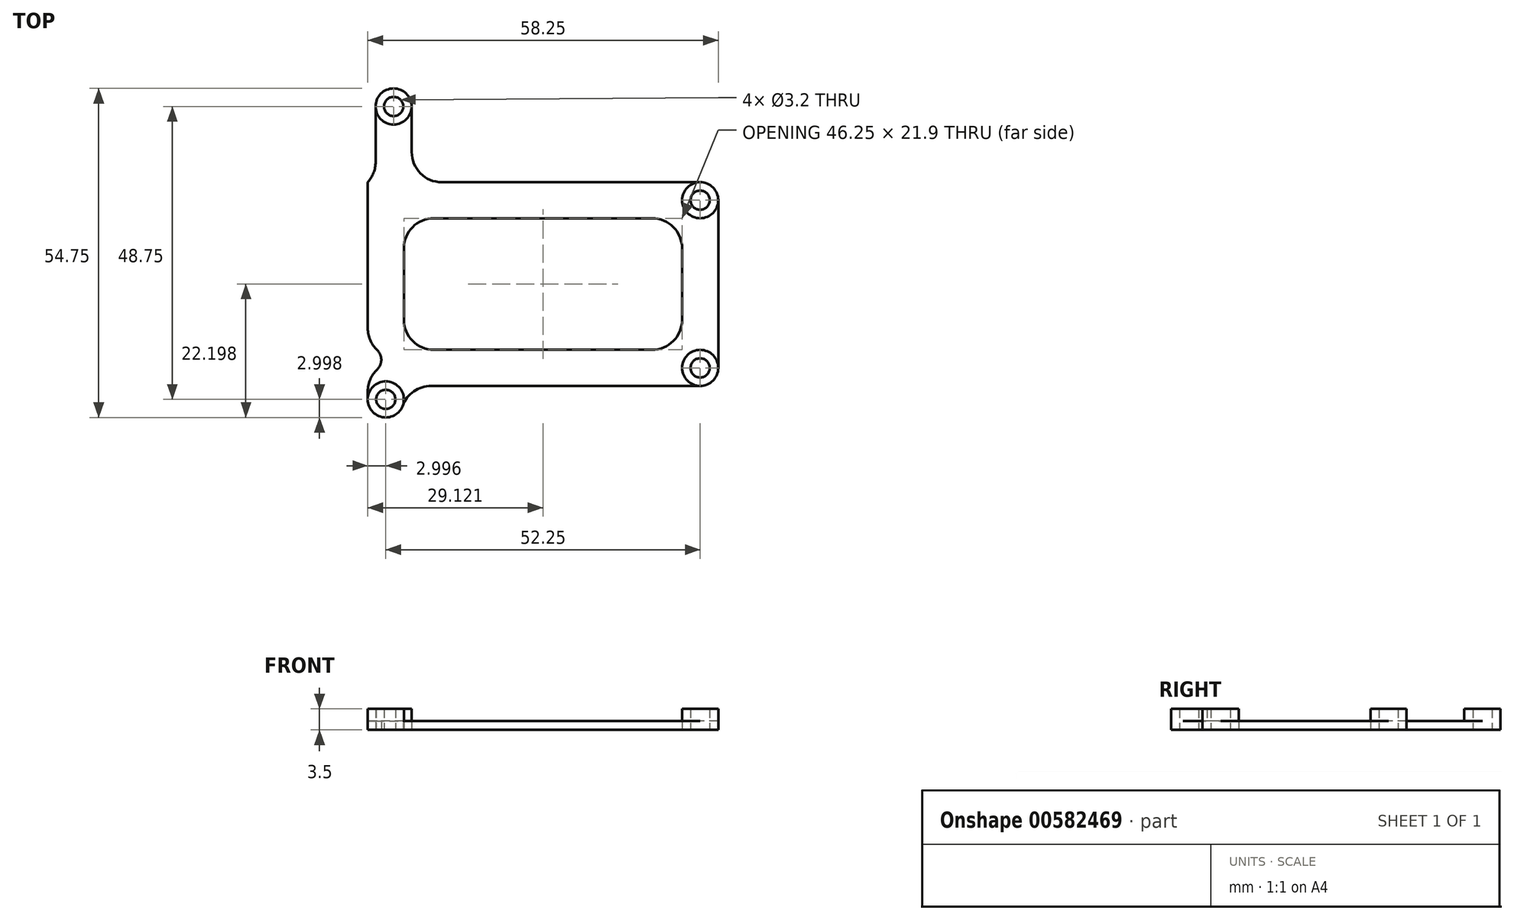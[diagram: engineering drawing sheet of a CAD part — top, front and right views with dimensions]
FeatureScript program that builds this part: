
annotation { "Feature Type Name" : "Feature", "Feature Type Description" : "" }
export const myFeature = defineFeature(function(context is Context, id is Id, definition is map)
    precondition{}
    {
        {
            var Q0;
            Q0=qCreatedBy(makeId("Top.planeOp"),FACE);
            var sketch = newSketch(context, id + "F0", { "sketchPlane" : qUnion([Q0])});
            skLineSegment(sketch, "E0.bottom", {"start": v(-21.9, 24.36) * mm, "end": v(30.35, 24.36) * mm, "construction": true});
            skLineSegment(sketch, "E0.top", {"start": v(-21.9, -24.4) * mm, "end": v(30.35, -24.4) * mm, "construction": true});
            skLineSegment(sketch, "E0.left", {"start": v(-21.9, 24.36) * mm, "end": v(-21.9, -24.4) * mm, "construction": true});
            skLineSegment(sketch, "E0.right", {"start": v(30.35, 24.36) * mm, "end": v(30.35, -24.4) * mm, "construction": true});
            skLineSegment(sketch, "E1", {"start": v(27.28, -19.14) * mm, "end": v(31.82, -19.14) * mm, "construction": true});
            skLineSegment(sketch, "E2", {"start": v(26.18, 8.76) * mm, "end": v(34.25, 8.76) * mm, "construction": true});
            skCircle(sketch, "E3", {"center": v(30.35, 8.76) * mm, "radius": 1.6 * mm});
            skCircle(sketch, "E4", {"center": v(30.35, -19.14) * mm, "radius": 1.6 * mm});
            skCircle(sketch, "E5", {"center": v(-21.9, -24.4) * mm, "radius": 1.6 * mm});
            skPoint(sketch, "E6.rect.middle", {"position": v(-21.9, 0) * mm});
            skLineSegment(sketch, "E7.bottom", {"start": v(30.35, 11.76) * mm, "end": v(-24.9, 11.76) * mm});
            skLineSegment(sketch, "E7.top", {"start": v(30.35, -22.14) * mm, "end": v(-18.9, -22.14) * mm});
            skLineSegment(sketch, "E7.left", {"start": v(33.35, 8.76) * mm, "end": v(33.35, -19.14) * mm});
            skLineSegment(sketch, "E7.right", {"start": v(-18.9, 11.76) * mm, "end": v(-18.9, -22.14) * mm});
            skLineSegment(sketch, "E8.bottom", {"start": v(-18.9, 5.76) * mm, "end": v(27.35, 5.76) * mm});
            skLineSegment(sketch, "E8.top", {"start": v(-18.9, -16.14) * mm, "end": v(27.35, -16.14) * mm});
            skLineSegment(sketch, "E8.left", {"start": v(-18.9, 5.76) * mm, "end": v(-18.9, -16.14) * mm});
            skLineSegment(sketch, "E8.right", {"start": v(27.35, 5.76) * mm, "end": v(27.35, -16.14) * mm});
            skCircle(sketch, "E9", {"center": v(-21.9, -24.4) * mm, "radius": 3 * mm});
            skCircle(sketch, "E10", {"center": v(30.35, 8.76) * mm, "radius": 3 * mm});
            skCircle(sketch, "E11", {"center": v(30.35, -19.14) * mm, "radius": 3 * mm});
            skLineSegment(sketch, "E12", {"start": v(-20.6, 24.36) * mm, "end": v(-20.6, 34.98) * mm, "construction": true});
            skCircle(sketch, "E13", {"center": v(-20.6, 24.36) * mm, "radius": 1.6 * mm});
            skPoint(sketch, "E14.orphan", {"position": v(-24.9, 28.63) * mm});
            skLineSegment(sketch, "E15.trimOffspring", {"start": v(-18.9, 11.76) * mm, "end": v(-18.9, -24.4) * mm});
            skPoint(sketch, "E6.rect.left.start.orphan", {"position": v(-18.9, 28.63) * mm});
            skCircle(sketch, "E16", {"center": v(-20.6, 24.36) * mm, "radius": 3 * mm});
            skLineSegment(sketch, "E17.top", {"start": v(-23.6, 11.76) * mm, "end": v(-17.6, 11.76) * mm});
            skLineSegment(sketch, "E17.left", {"start": v(-23.6, 24.36) * mm, "end": v(-23.6, 11.76) * mm});
            skLineSegment(sketch, "E17.right", {"start": v(-17.6, 24.36) * mm, "end": v(-17.6, 11.76) * mm});
            skLineSegment(sketch, "E18", {"start": v(-24.9, -24.4) * mm, "end": v(-24.9, -20.04) * mm});
            skPoint(sketch, "E19.orphan", {"position": v(-24.9, -28.63) * mm});
            skPoint(sketch, "E20.orphan", {"position": v(-18.9, -28.63) * mm});
            skArc(sketch, "E21", {"start": v(-24.9, -20.04) * mm, "mid": v(-22.65, -17.8) * mm, "end": v(-24.9, -15.54) * mm});
            skLineSegment(sketch, "E22.trimOffspring", {"start": v(-24.9, -15.54) * mm, "end": v(-24.9, 11.76) * mm});
            skLineSegment(sketch, "E23", {"start": v(-24.9, -17.8) * mm, "end": v(-26, -17.8) * mm, "construction": true});
            skLineSegment(sketch, "E24", {"start": v(-21.9, -21.4) * mm, "end": v(-27.02, -21.4) * mm, "construction": true});
            skSolve(sketch);
        }
        {
            var Q0;
            {var subQ8=sQuery(id+"F0.wireOp",EDGE,"E8.left");Q0=makeQuery(id+"F0.imprint","IMPRINT",FACE,{"disambiguationData":[TD([[makeQuery(id+"F0.imprint","IMPRINT",EDGE,{"derivedFrom":subQ8}),-1.0]])]});}
            var Q1;
            {var subQ9=sQuery(id+"F0.wireOp",EDGE,"E8.bottom");Q1=makeQuery(id+"F0.imprint","IMPRINT",FACE,{"disambiguationData":[TD([[makeQuery(id+"F0.imprint","IMPRINT",EDGE,{"derivedFrom":subQ9}),1.0]])]});}
            var Q2;
            Q2=makeQuery(id+"F0.imprint","IMPRINT",FACE,{"disambiguationData":[TD([[makeQuery(id+"F0.imprint","IMPRINT",EDGE,{"derivedFrom":sQuery(id+"F0.wireOp",EDGE,"617df2c3-c054-49b6-bbc8-ea8e598be705")}),-1.0]])]});
            var Q3;
            Q3=makeQuery(id+"F0.imprint","IMPRINT",FACE,{"disambiguationData":[TD([[makeQuery(id+"F0.imprint","IMPRINT",EDGE,{"derivedFrom":sQuery(id+"F0.wireOp",EDGE,"E5")}),-1.0]])]});
            var Q4;
            Q4=makeQuery(id+"F0.imprint","IMPRINT",FACE,{"disambiguationData":[TD([[makeQuery(id+"F0.imprint","IMPRINT",EDGE,{"derivedFrom":sQuery(id+"F0.wireOp",EDGE,"E4")}),-1.0]])]});
            var Q5;
            Q5=makeQuery(id+"F0.imprint","IMPRINT",FACE,{"disambiguationData":[TD([[makeQuery(id+"F0.imprint","IMPRINT",EDGE,{"derivedFrom":sQuery(id+"F0.wireOp",EDGE,"E3")}),-1.0]])]});
            var Q6;
            {var subQ0=sQuery(id+"F0.wireOp",EDGE,"E17.left");var subQ1=sQuery(id+"F0.wireOp",EDGE,"E16");var subQ2=makeQuery(id+"F0.imprint","INTERSECT",VERTEX,{"derivedFrom":[subQ1,subQ0]});Q6=makeQuery(id+"F0.imprint","IMPRINT",FACE,{"disambiguationData":[TD([[makeQuery(id+"F0.imprint","IMPRINT",EDGE,{"disambiguationData":[TD([[subQ2,-1.0]])],"derivedFrom":subQ1}),-1.0]])]});}
            var Q7;
            Q7=makeQuery(id+"F0.imprint","IMPRINT",FACE,{"disambiguationData":[TD([[makeQuery(id+"F0.imprint","IMPRINT",EDGE,{"derivedFrom":sQuery(id+"F0.wireOp",EDGE,"E13")}),-1.0]])]});
            var Q8;
            {var subQ1=sQuery(id+"F0.wireOp",EDGE,"E7.bottom");var subQ10=sQuery(id+"F0.wireOp",EDGE,"E6.rect.right");var subQ12=makeQuery(id+"F0.imprint","INTERSECT",VERTEX,{"derivedFrom":[subQ10,subQ1]});Q8=makeQuery(id+"F0.imprint","IMPRINT",FACE,{"disambiguationData":[TD([[makeQuery(id+"F0.imprint","IMPRINT",EDGE,{"disambiguationData":[TD([[subQ12,-1.0]])],"derivedFrom":subQ10}),1.0]])]});}
            var Q9;
            {var subQ10=sQuery(id+"F0.wireOp",EDGE,"E18");Q9=makeQuery(id+"F0.imprint","IMPRINT",FACE,{"disambiguationData":[TD([[makeQuery(id+"F0.imprint","IMPRINT",EDGE,{"derivedFrom":subQ10}),-1.0]])]});}
            extrude(context, id + "F1", {"entities" : qUnion([Q0, Q1, Q2, Q3, Q4, Q5, Q6, Q7, Q8, Q9]), "depth" : 1.5 * mm});
        }
        {
            var Q0;
            Q0=makeQuery(id+"F0.imprint","IMPRINT",FACE,{"disambiguationData":[TD([[makeQuery(id+"F0.imprint","IMPRINT",EDGE,{"derivedFrom":sQuery(id+"F0.wireOp",EDGE,"E5")}),-1.0]])]});
            var Q1;
            Q1=makeQuery(id+"F0.imprint","IMPRINT",FACE,{"disambiguationData":[TD([[makeQuery(id+"F0.imprint","IMPRINT",EDGE,{"derivedFrom":sQuery(id+"F0.wireOp",EDGE,"E3")}),-1.0]])]});
            var Q2;
            Q2=makeQuery(id+"F0.imprint","IMPRINT",FACE,{"disambiguationData":[TD([[makeQuery(id+"F0.imprint","IMPRINT",EDGE,{"derivedFrom":sQuery(id+"F0.wireOp",EDGE,"E4")}),-1.0]])]});
            var Q3;
            Q3=makeQuery(id+"F0.imprint","IMPRINT",FACE,{"disambiguationData":[TD([[makeQuery(id+"F0.imprint","IMPRINT",EDGE,{"derivedFrom":sQuery(id+"F0.wireOp",EDGE,"E13")}),-1.0]])]});
            extrude(context, id + "F2", {"entities" : qUnion([Q0, Q1, Q2, Q3]), "operationType" : NewBodyOperationType.ADD, "depth" : 3.5 * mm});
        }
        {
            var Q0;
            Q0=makeQuery(id+"F1.opExtrude","SWEPT_EDGE",EDGE,{"disambiguationData":[OSD([sQuery(id+"F0.wireOp",EDGE,"E7.right"),sQuery(id+"F0.wireOp",EDGE,"E8.bottom"),sQuery(id+"F0.wireOp",EDGE,"E8.left")])]});
            var Q1;
            Q1=makeQuery(id+"F1.opExtrude","SWEPT_EDGE",EDGE,{"disambiguationData":[OSD([sQuery(id+"F0.wireOp",EDGE,"E7.right"),sQuery(id+"F0.wireOp",EDGE,"E8.top"),sQuery(id+"F0.wireOp",EDGE,"E8.left")])]});
            var Q2;
            Q2=makeQuery(id+"F1.opExtrude","SWEPT_EDGE",EDGE,{"disambiguationData":[OSD([sQuery(id+"F0.wireOp",EDGE,"E8.bottom"),sQuery(id+"F0.wireOp",EDGE,"E8.right")])]});
            var Q3;
            Q3=makeQuery(id+"F1.opExtrude","SWEPT_EDGE",EDGE,{"disambiguationData":[OSD([sQuery(id+"F0.wireOp",EDGE,"E8.top"),sQuery(id+"F0.wireOp",EDGE,"E8.right")])]});
            var Q4;
            Q4=makeQuery(id+"F1.opExtrude","SWEPT_EDGE",EDGE,{"disambiguationData":[OSD([sQuery(id+"F0.wireOp",EDGE,"E7.bottom"),sQuery(id+"F0.wireOp",EDGE,"E17.top"),sQuery(id+"F0.wireOp",EDGE,"E17.right")])]});
            var Q5;
            Q5=makeQuery(id+"F1.opExtrude","SWEPT_EDGE",EDGE,{"disambiguationData":[OSD([sQuery(id+"F0.wireOp",EDGE,"E7.bottom"),sQuery(id+"F0.wireOp",EDGE,"E17.top"),sQuery(id+"F0.wireOp",EDGE,"E17.left")])]});
            var Q6;
            Q6=makeQuery(id+"F1.opExtrude","SWEPT_EDGE",EDGE,{"disambiguationData":[OSD([sQuery(id+"F0.wireOp",EDGE,"E7.top"),sQuery(id+"F0.wireOp",EDGE,"E15.trimOffspring")])]});
            fillet(context, id + "F3", {"entities" : qUnion([Q0, Q1, Q2, Q3, Q4, Q5, Q6]), "radius" : 5 * mm, "tangentPropagation" : true, "allowEdgeOverflow" : false});
        }
        {
            var Q0;
            Q0=makeQuery(id+"F1.opExtrude","SWEPT_EDGE",EDGE,{"disambiguationData":[OSD([sQuery(id+"F0.wireOp",EDGE,"E21"),sQuery(id+"F0.wireOp",EDGE,"E22.trimOffspring")])]});
            var Q1;
            Q1=makeQuery(id+"F1.opExtrude","SWEPT_EDGE",EDGE,{"disambiguationData":[OSD([sQuery(id+"F0.wireOp",EDGE,"E18"),sQuery(id+"F0.wireOp",EDGE,"E21")])]});
            fillet(context, id + "F4", {"entities" : qUnion([Q0, Q1]), "radius" : 5 * mm, "tangentPropagation" : true, "allowEdgeOverflow" : false});
        }
    });
